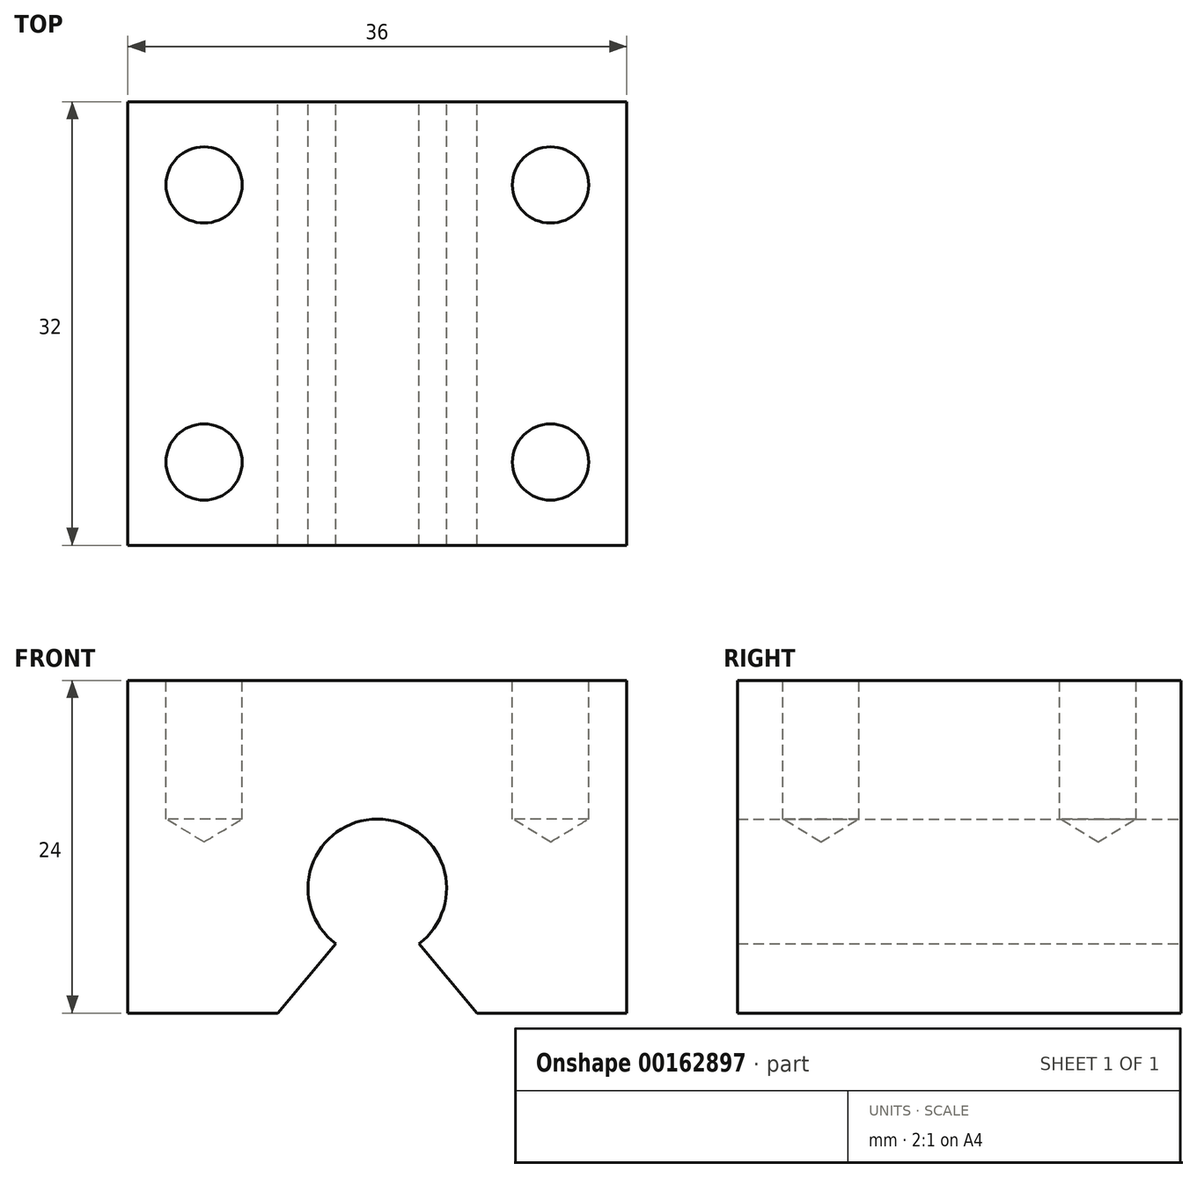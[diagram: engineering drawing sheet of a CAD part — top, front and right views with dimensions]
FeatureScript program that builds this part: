
annotation { "Feature Type Name" : "Feature", "Feature Type Description" : "" }
export const myFeature = defineFeature(function(context is Context, id is Id, definition is map)
    precondition{}
    {
        {
            var Q0;
            Q0=qCreatedBy(makeId("Front.planeOp"),FACE);
            var sketch = newSketch(context, id + "F0", { "sketchPlane" : qUnion([Q0])});
            skArc(sketch, "E0", {"start": v(3, -4) * mm, "mid": v(0, 5) * mm, "end": v(-3, -4) * mm});
            skLineSegment(sketch, "E1.bottom", {"start": v(18, -9) * mm, "end": v(7.2, -9) * mm});
            skLineSegment(sketch, "E1.top", {"start": v(18, 15) * mm, "end": v(-18, 15) * mm});
            skLineSegment(sketch, "E1.left", {"start": v(18, -9) * mm, "end": v(18, 15) * mm});
            skLineSegment(sketch, "E1.right", {"start": v(-18, -9) * mm, "end": v(-18, 15) * mm});
            skPoint(sketch, "E1.middle", {"position": v(0, 3) * mm});
            skLineSegment(sketch, "E2", {"start": v(-3, -4) * mm, "end": v(-7.2, -9) * mm});
            skLineSegment(sketch, "E3.MirrorCS", {"start": v(3, -4) * mm, "end": v(7.2, -9) * mm});
            skLineSegment(sketch, "E4.trimOffspring", {"start": v(-7.2, -9) * mm, "end": v(-18, -9) * mm});
            skSolve(sketch);
        }
        {
            var Q0;
            Q0=makeQuery(id+"F0.imprint","IMPRINT",FACE,{"disambiguationData":[TD([[makeQuery(id+"F0.imprint","IMPRINT",EDGE,{"derivedFrom":sQuery(id+"F0.wireOp",EDGE,"E0")}),-1.0]])]});
            extrude(context, id + "F1", {"entities" : qUnion([Q0]), "endBound" : BoundingType.SYMMETRIC, "depth" : 32 * mm});
        }
        {
            var Q0;
            Q0=makeQuery(id+"F1.opExtrude","SWEPT_FACE",FACE,{"disambiguationData":[OSD([sQuery(id+"F0.wireOp",EDGE,"E1.top")])]});
            var sketch = newSketch(context, id + "F2", { "sketchPlane" : qUnion([Q0])});
            skLineSegment(sketch, "E5.bottom", {"start": v(12.5, -10) * mm, "end": v(-12.5, -10) * mm, "construction": true});
            skLineSegment(sketch, "E5.top", {"start": v(12.5, 10) * mm, "end": v(-12.5, 10) * mm, "construction": true});
            skLineSegment(sketch, "E5.left", {"start": v(12.5, -10) * mm, "end": v(12.5, 10) * mm, "construction": true});
            skLineSegment(sketch, "E5.right", {"start": v(-12.5, -10) * mm, "end": v(-12.5, 10) * mm, "construction": true});
            skPoint(sketch, "E5.middle", {"position": v(0, 0) * mm});
            skSolve(sketch);
        }
        {
            var Q0;
            Q0=sQuery(id+"F2.wireOp",VERTEX,"E5.top.end");
            var Q1;
            Q1=sQuery(id+"F2.wireOp",VERTEX,"E5.right.start");
            var Q2;
            Q2=sQuery(id+"F2.wireOp",VERTEX,"E5.left.start");
            var Q3;
            Q3=sQuery(id+"F2.wireOp",VERTEX,"E5.left.end");
            var Q4;
            Q4=makeQuery(id+"F1.opExtrude","SWEPT_BODY",BODY,{"disambiguationData":[OSD([sQuery(id+"F0.wireOp",EDGE,"E0"),sQuery(id+"F0.wireOp",EDGE,"E1.bottom"),sQuery(id+"F0.wireOp",EDGE,"E1.top"),sQuery(id+"F0.wireOp",EDGE,"E1.left"),sQuery(id+"F0.wireOp",EDGE,"E1.right"),sQuery(id+"F0.wireOp",EDGE,"E2"),sQuery(id+"F0.wireOp",EDGE,"E3.MirrorCS"),sQuery(id+"F0.wireOp",EDGE,"E4.trimOffspring")])]});
            hole(context, id + "F3", {"style" : HoleStyle.SIMPLE, "endStyle" : HoleEndStyle.BLIND, "standardTappedOrClearance" : lookupTablePath({ "standard" : "ISO", "fit" : "Normal", "size" : "M5", "type" : "Clearance" }), "standardBlindInLast" : lookupTablePath({ "fit" : "Standard", "standard" : "ISO", "size" : "M5", "type" : "Clearance" }), "holeDiameter" : 5.5 * mm, "holeDepth" : 10 * mm, "startFromSketch" : true, "locations" : qUnion([Q0, Q1, Q2, Q3]), "scope" : qUnion([Q4])});
        }
    });
